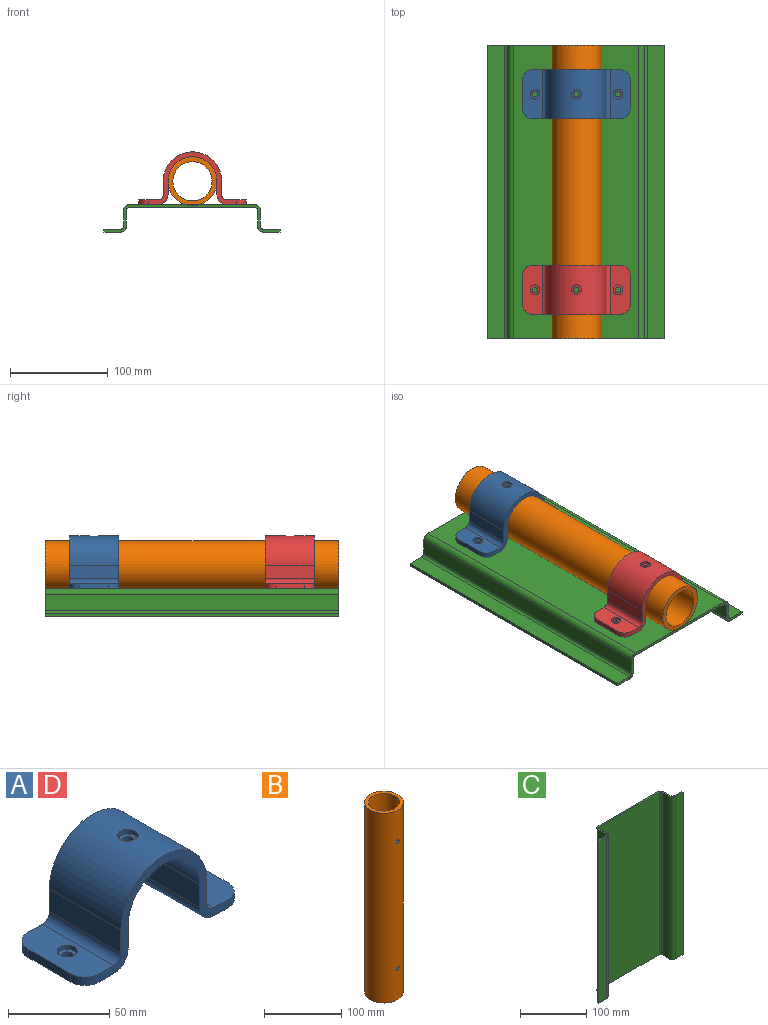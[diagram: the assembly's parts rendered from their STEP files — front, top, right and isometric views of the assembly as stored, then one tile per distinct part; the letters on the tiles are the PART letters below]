
ASSEMBLY  parts=4 mates=6
PART A: 31 faces, bbox 110x50x54 mm
  f0: cylinder r=30mm len=60mm, axis (0,1,0), area 4633.7mm2, adj f2,f3,f12,f13,f14
  f1: cylinder r=25mm len=50mm, axis (0,1,0), area 3903.2mm2, adj f7,f8,f12,f13,f15
  f2: plane 50x14mm, normal (1,0,0), area 700mm2, adj f0,f12,f13,f24
  f3: plane 50x14mm, normal (-1,0,0), area 700mm2, adj f0,f12,f13,f23
  f4: plane 50x20mm, normal (0,0,1), area 878.5mm2, adj f5,f12,f13,f19,f23,f28,f30
  f5: plane 30x5mm, normal (-1,0,0), area 150mm2, adj f4,f6,f28,f30
  f6: plane 50x20mm, normal (0,0,-1), area 933.3mm2, adj f5,f12,f13,f17,f25,f28,f30
  f7: plane 50x14mm, normal (1,0,0), area 700mm2, adj f1,f12,f13,f25
  f8: plane 50x14mm, normal (-1,0,0), area 700mm2, adj f1,f12,f13,f26
  f9: plane 50x20mm, normal (0,0,-1), area 933.3mm2, adj f10,f12,f13,f20,f26,f27,f29
  f10: plane 30x5mm, normal (1,0,0), area 150mm2, adj f9,f11,f27,f29
  f11: plane 50x20mm, normal (0,0,1), area 878.5mm2, adj f10,f12,f13,f22,f24,f27,f29
  f12: plane 90x54mm, normal (0,-1,0), area 789.8mm2, adj f0,f1,f2,f3,f4,f6,f7,f8
  f13: plane 90x54mm, normal (0,1,0), area 789.8mm2, adj f0,f1,f2,f3,f4,f6,f7,f8
  f14: cylinder r=5mm len=10mm, axis (0,0,1), area 85.1mm2, adj f0,f16
  f15: cylinder r=2.75mm len=5.5mm, axis (0,0,1), area 37.3mm2, adj f1,f16
  f16: plane 10x10mm, normal (0,0,1), area 54.8mm2, adj f14,f15
  f17: cylinder r=2.75mm len=5.5mm, axis (0,0,1), area 43.2mm2, adj f6,f18
  f18: plane 10x10mm, normal (0,0,1), area 54.8mm2, adj f17,f19
  f19: cylinder r=5mm len=10mm, axis (0,0,1), area 78.5mm2, adj f4,f18
  f20: cylinder r=2.75mm len=5.5mm, axis (0,0,1), area 43.2mm2, adj f9,f21
  f21: plane 10x10mm, normal (0,0,1), area 54.8mm2, adj f20,f22
  f22: cylinder r=5mm len=10mm, axis (0,0,1), area 78.5mm2, adj f11,f21
  f23: cylinder r=5mm len=50mm, axis (0,-1,0), area 392.7mm2, adj f3,f4,f12,f13
  f24: cylinder r=5mm len=50mm, axis (0,-1,0), area 392.7mm2, adj f2,f11,f12,f13
  f25: cylinder r=10mm len=50mm, axis (0,1,0), area 785.4mm2, adj f6,f7,f12,f13
  f26: cylinder r=10mm len=50mm, axis (0,1,0), area 785.4mm2, adj f8,f9,f12,f13
  f27: cylinder r=10mm len=10mm, axis (0,0,1), area 78.5mm2, adj f9,f10,f11,f13
  f28: cylinder r=10mm len=10mm, axis (0,0,-1), area 78.5mm2, adj f4,f5,f6,f13
  f29: cylinder r=10mm len=10mm, axis (0,0,-1), area 78.5mm2, adj f9,f10,f11,f12
  f30: cylinder r=10mm len=10mm, axis (0,0,1), area 78.5mm2, adj f4,f5,f6,f12
PART B: 8 faces, bbox 50x50x300 mm
  f0: cylinder r=25mm len=300mm, axis (0,0,-1), area 47028.4mm2, adj f2,f3,f4,f5,f6,f7
  f1: cylinder r=20mm len=300mm, axis (0,0,-1), area 37603.4mm2, adj f2,f3,f4,f5,f6,f7
  f2: plane 50x50mm, normal (0,0,1), area 706.9mm2, adj f0,f1
  f3: plane 50x50mm, normal (0,0,-1), area 706.9mm2, adj f0,f1
  f4: cylinder r=2.75mm len=5.5mm, axis (0,1,0), area 86.7mm2, adj f0,f1
  f5: cylinder r=2.75mm len=5.5mm, axis (0,1,0), area 86.7mm2, adj f0,f1
  f6: cylinder r=2.75mm len=5.5mm, axis (0,1,0), area 86.7mm2, adj f0,f1
  f7: cylinder r=2.75mm len=5.5mm, axis (0,1,0), area 86.7mm2, adj f0,f1
PART C: 22 faces, bbox 180x28x300 mm
  f0: plane 180x28mm, normal (0,0,1), area 666.8mm2, adj f2,f3,f4,f5,f6,f7,f8,f9
  f1: plane 180x28mm, normal (0,0,-1), area 666.8mm2, adj f2,f3,f4,f5,f6,f7,f8,f9
  f2: plane 300x17mm, normal (0,-1,0), area 5100mm2, adj f0,f1,f5,f19
  f3: plane 300x16mm, normal (-1,0,0), area 4800mm2, adj f0,f1,f16,f21
  f4: plane 300x17mm, normal (0,1,0), area 5100mm2, adj f0,f1,f5,f16
  f5: plane 300x3mm, normal (-1,0,0), area 900mm2, adj f0,f1,f2,f4
  f6: plane 300x17mm, normal (0,-1,0), area 5100mm2, adj f0,f1,f7,f18
  f7: plane 300x3mm, normal (1,0,0), area 900mm2, adj f0,f1,f6,f8
  f8: plane 300x17mm, normal (0,1,0), area 5100mm2, adj f0,f1,f7,f17
  f9: plane 300x16mm, normal (1,0,0), area 4800mm2, adj f0,f1,f17,f20
  f10: plane 300x128mm, normal (0,1,0), area 38400mm2, adj f0,f1,f20,f21
  f11: plane 300x16mm, normal (1,0,0), area 4800mm2, adj f0,f1,f15,f19
  f12: plane 300x16mm, normal (-1,0,0), area 4800mm2, adj f0,f1,f14,f18
  f13: plane 300x128mm, normal (0,-1,0), area 38400mm2, adj f0,f1,f14,f15
  f14: cylinder r=3mm len=300mm, axis (0,0,-1), area 1413.7mm2, adj f0,f1,f12,f13
  f15: cylinder r=3mm len=300mm, axis (0,0,1), area 1413.7mm2, adj f0,f1,f11,f13
  f16: cylinder r=3mm len=300mm, axis (0,0,1), area 1413.7mm2, adj f0,f1,f3,f4
  f17: cylinder r=3mm len=300mm, axis (0,0,-1), area 1413.7mm2, adj f0,f1,f8,f9
  f18: cylinder r=6mm len=300mm, axis (0,0,1), area 2827.4mm2, adj f0,f1,f6,f12
  f19: cylinder r=6mm len=300mm, axis (0,0,-1), area 2827.4mm2, adj f0,f1,f2,f11
  f20: cylinder r=6mm len=300mm, axis (0,0,1), area 2827.4mm2, adj f0,f1,f9,f10
  f21: cylinder r=6mm len=300mm, axis (0,0,-1), area 2827.4mm2, adj f0,f1,f3,f10
PART D: same geometry as A
PLACE A t=(-146.11,116.76,41.47)mm
PLACE B rot(axis=(1,0,0),90deg) t=(-146.11,16.76,41.47)mm
PLACE C rot(axis=(1,0,0),90deg) t=(-186.6,16.76,-10.53)mm
PLACE D t=(-146.11,-83.24,41.47)mm fixed
MATE planar C.f10 <-> A.f30  axis (0,0,1) through (-146.6,16.76,17.47)mm
MATE planar C.f1 <-> B.f0  axis (0,1,0) through (-146.6,166.76,8.76)mm
MATE slider B.f0 <-> A.f0  axis (0,1,0) through (-146.11,16.76,41.47)mm
MATE slider A.f14 <-> B.f6  axis (0,0,1) through (-146.11,116.76,68.55)mm
MATE cylindrical B.f0 <-> D.f0  axis (0,1,0) through (-146.11,16.76,41.47)mm
MATE slider B.f4 <-> D.f14  axis (0,0,1) through (-146.11,-83.24,66.51)mm
